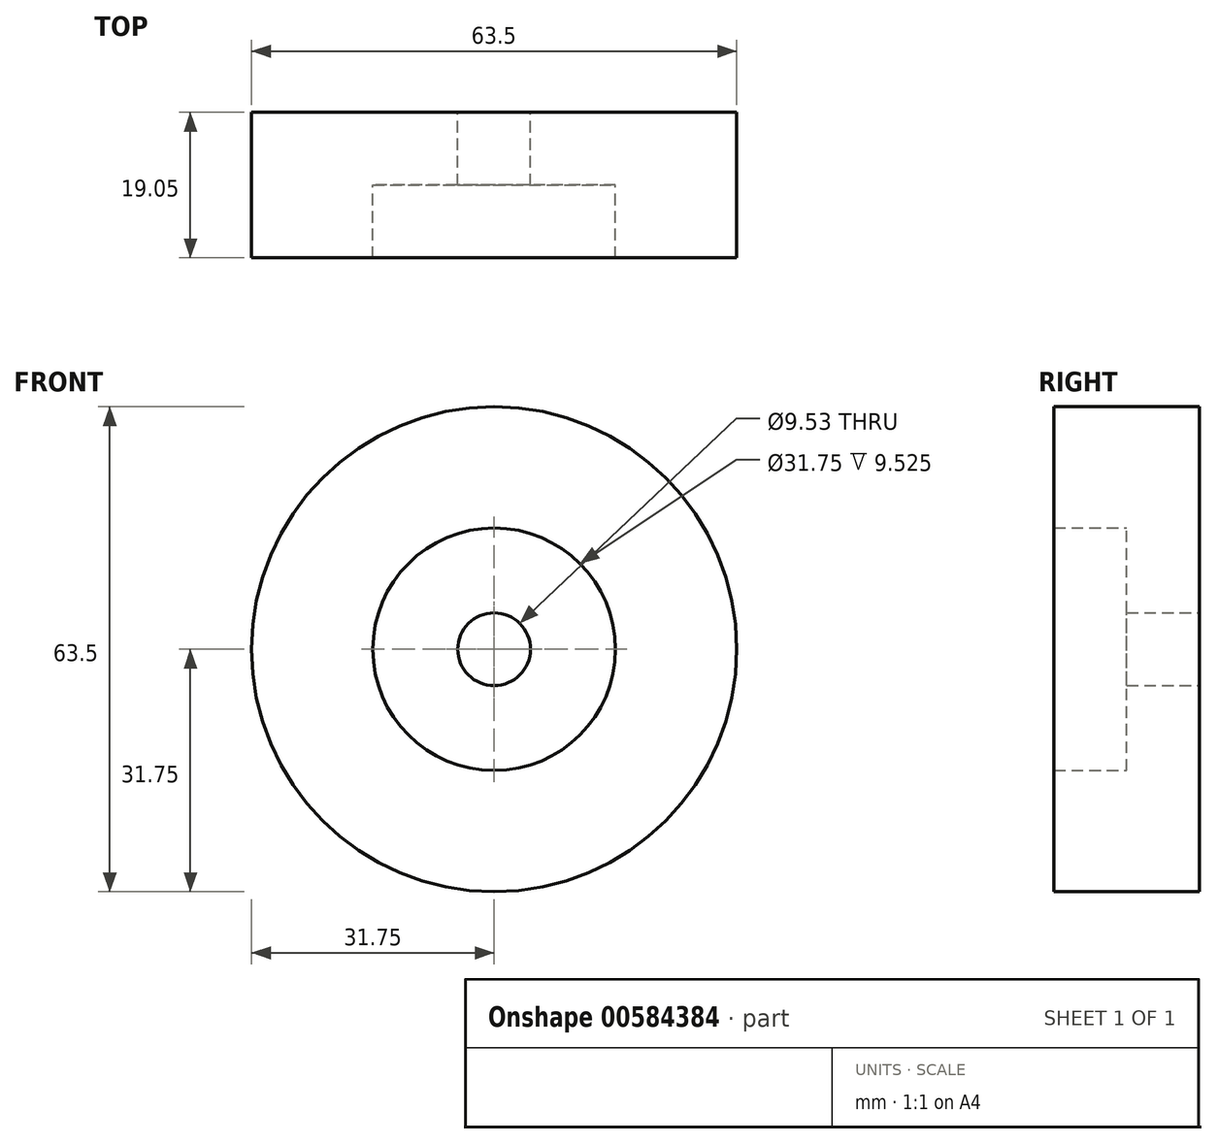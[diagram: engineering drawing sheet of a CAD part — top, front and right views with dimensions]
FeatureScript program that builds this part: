
annotation { "Feature Type Name" : "Feature", "Feature Type Description" : "" }
export const myFeature = defineFeature(function(context is Context, id is Id, definition is map)
    precondition{}
    {
        {
            var Q0;
            Q0=qCreatedBy(makeId("Front.planeOp"),FACE);
            var sketch = newSketch(context, id + "F0", { "sketchPlane" : qUnion([Q0])});
            skCircle(sketch, "E0", {"center": v(0, 0) * mm, "radius": 31.75 * mm});
            skCircle(sketch, "E1", {"center": v(0, 0) * mm, "radius": 15.88 * mm});
            skCircle(sketch, "E2", {"center": v(0, 0) * mm, "radius": 4.76 * mm});
            skSolve(sketch);
        }
        {
            var Q0;
            Q0=makeQuery(id+"F0.imprint","IMPRINT",FACE,{"disambiguationData":[TD([[makeQuery(id+"F0.imprint","IMPRINT",EDGE,{"derivedFrom":sQuery(id+"F0.wireOp",EDGE,"E1")}),1.0]])]});
            extrude(context, id + "F1", {"entities" : qUnion([Q0]), "depth" : 9.52 * mm, "offsetDistance" : 25.4 * mm});
        }
        {
            var Q0;
            Q0 = qSketchRegion(id + "F0", true);
            extrude(context, id + "F2", {"entities" : qUnion([Q0]), "operationType" : NewBodyOperationType.ADD, "depth" : 19.05 * mm, "offsetDistance" : 25.4 * mm});
        }
    });
